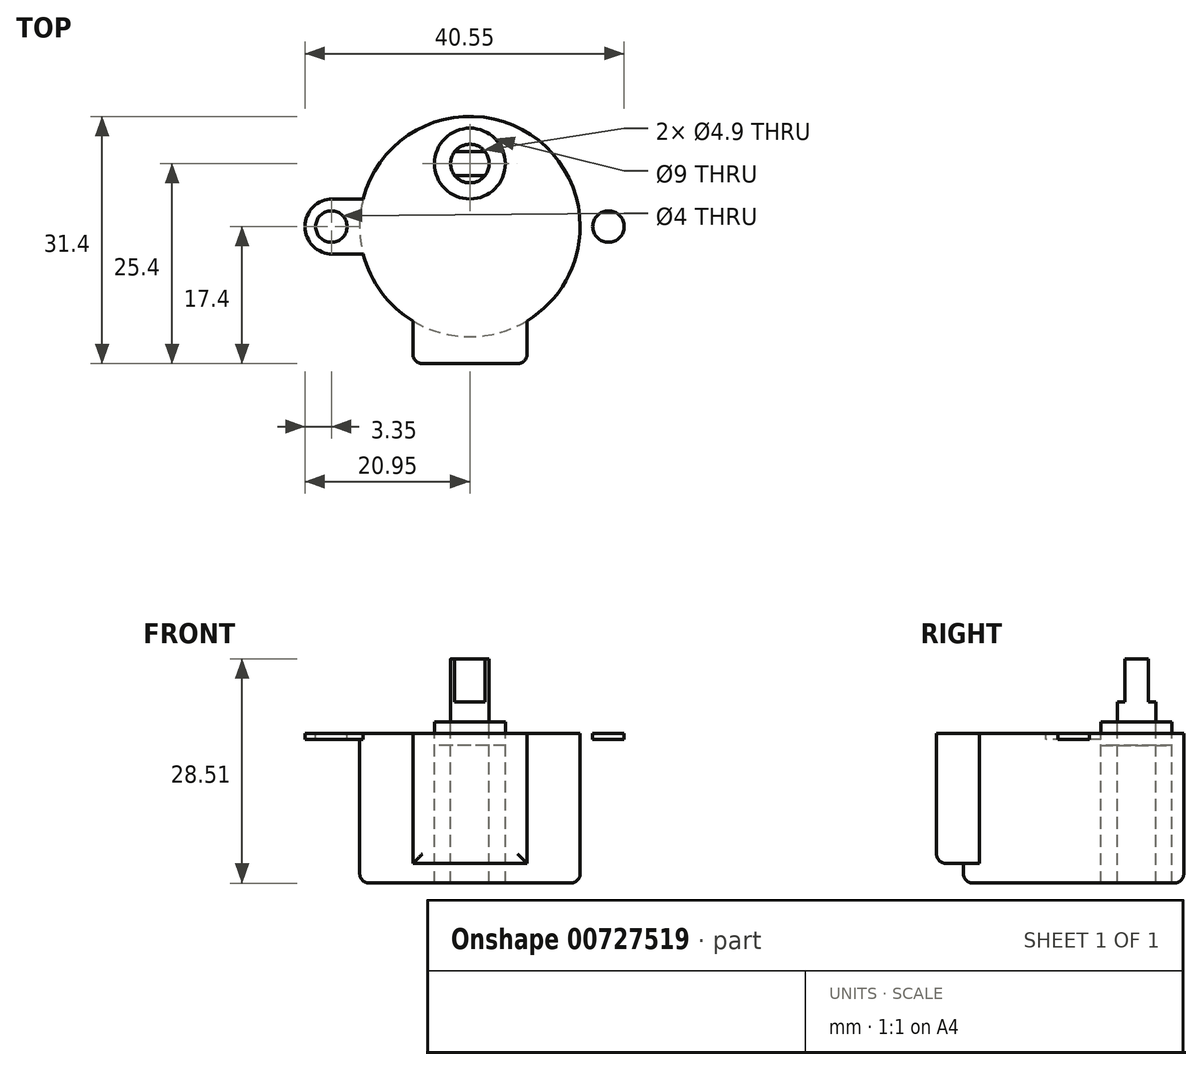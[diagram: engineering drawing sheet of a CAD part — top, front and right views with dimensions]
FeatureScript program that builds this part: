
annotation { "Feature Type Name" : "Feature", "Feature Type Description" : "" }
export const myFeature = defineFeature(function(context is Context, id is Id, definition is map)
    precondition{}
    {
        {
            var Q0;
            Q0=qCreatedBy(makeId("Top.planeOp"),FACE);
            var sketch = newSketch(context, id + "F0", { "sketchPlane" : qUnion([Q0])});
            skCircle(sketch, "E0", {"center": v(0, 0) * mm, "radius": 14 * mm});
            skPoint(sketch, "E1", {"position": v(0, 8) * mm});
            skCircle(sketch, "E2", {"center": v(0, 8) * mm, "radius": 4.5 * mm});
            skLineSegment(sketch, "E3.bottom", {"start": v(-17.45, -3.5) * mm, "end": v(-13.56, -3.5) * mm});
            skLineSegment(sketch, "E3.top", {"start": v(-17.45, 3.5) * mm, "end": v(-13.56, 3.5) * mm});
            skLineSegment(sketch, "E3.left", {"start": v(-20.95, 0) * mm, "end": v(-20.95, 0) * mm});
            skLineSegment(sketch, "E3.right", {"start": v(20.95, 0) * mm, "end": v(20.95, 0) * mm});
            skCircle(sketch, "E4", {"center": v(-17.6, 0) * mm, "radius": 2 * mm});
            skPoint(sketch, "E5.visualSharp", {"position": v(-20.95, 3.5) * mm});
            skArc(sketch, "E5.filletArc", {"start": v(-17.45, 3.5) * mm, "mid": v(-19.92, 2.47) * mm, "end": v(-20.95, 0) * mm});
            skPoint(sketch, "E6.visualSharp", {"position": v(-20.95, -3.5) * mm});
            skArc(sketch, "E6.filletArc", {"start": v(-20.95, 0) * mm, "mid": v(-19.92, -2.47) * mm, "end": v(-17.45, -3.5) * mm});
            skCircle(sketch, "E7.MirrorC", {"center": v(17.6, 0) * mm, "radius": 2 * mm});
            skArc(sketch, "E8.MirrorCS", {"start": v(20.95, 0) * mm, "mid": v(19.92, -2.47) * mm, "end": v(17.45, -3.5) * mm});
            skArc(sketch, "E9.MirrorCS", {"start": v(17.45, 3.5) * mm, "mid": v(19.92, 2.47) * mm, "end": v(20.95, 0) * mm});
            skPoint(sketch, "E10.visualSharp", {"position": v(20.95, -3.5) * mm});
            skArc(sketch, "E10.filletArc", {"start": v(17.45, -3.5) * mm, "mid": v(19.92, -2.47) * mm, "end": v(20.95, 0) * mm});
            skPoint(sketch, "E11.visualSharp", {"position": v(20.95, 3.5) * mm});
            skArc(sketch, "E11.filletArc", {"start": v(20.95, 0) * mm, "mid": v(19.92, 2.47) * mm, "end": v(17.45, 3.5) * mm});
            skCircle(sketch, "E12", {"center": v(0, 8) * mm, "radius": 2.45 * mm});
            skLineSegment(sketch, "E13.bottom", {"start": v(1.94, 6.5) * mm, "end": v(-1.94, 6.5) * mm});
            skLineSegment(sketch, "E13.top", {"start": v(1.94, 9.5) * mm, "end": v(-1.94, 9.5) * mm});
            skLineSegment(sketch, "E14.trimOffspring", {"start": v(13.56, -3.5) * mm, "end": v(17.45, -3.5) * mm});
            skLineSegment(sketch, "E15.trimOffspring", {"start": v(13.56, 3.5) * mm, "end": v(17.45, 3.5) * mm});
            skPoint(sketch, "E16", {"position": v(0, -17.4) * mm});
            skLineSegment(sketch, "E17.bottom", {"start": v(0, -17.4) * mm, "end": v(7.25, -17.4) * mm});
            skLineSegment(sketch, "E17.right", {"start": v(7.25, -17.4) * mm, "end": v(7.25, -11.98) * mm});
            skLineSegment(sketch, "E18.MirrorCS", {"start": v(0, -17.4) * mm, "end": v(-7.25, -17.4) * mm});
            skLineSegment(sketch, "E19.MirrorCS", {"start": v(-7.25, -17.4) * mm, "end": v(-7.25, -11.98) * mm});
            skPoint(sketch, "E20.orphan", {"position": v(0, -11.4) * mm});
            skPoint(sketch, "E21.orphan", {"position": v(-7.25, -11.4) * mm});
            skPoint(sketch, "E22.orphan", {"position": v(7.25, -11.4) * mm});
            skSolve(sketch);
        }
        {
            var Q0;
            {var subQ0=sQuery(id+"F0.wireOp",EDGE,"E13.bottom");Q0=makeQuery(id+"F0.imprint","IMPRINT",FACE,{"disambiguationData":[TD([[makeQuery(id+"F0.imprint","IMPRINT",EDGE,{"derivedFrom":subQ0}),-1.0]])]});}
            extrude(context, id + "F1", {"entities" : qUnion([Q0]), "depth" : 8 * mm, "offsetDistance" : 25 * mm});
        }
        {
            var Q0;
            {var subQ0=sQuery(id+"F0.wireOp",EDGE,"E13.bottom");Q0=makeQuery(id+"F0.imprint","IMPRINT",FACE,{"disambiguationData":[TD([[makeQuery(id+"F0.imprint","IMPRINT",EDGE,{"derivedFrom":subQ0}),1.0]])]});}
            var Q1;
            {var subQ0=sQuery(id+"F0.wireOp",EDGE,"E13.top");Q1=makeQuery(id+"F0.imprint","IMPRINT",FACE,{"disambiguationData":[TD([[makeQuery(id+"F0.imprint","IMPRINT",EDGE,{"derivedFrom":subQ0}),-1.0]])]});}
            extrude(context, id + "F2", {"entities" : qUnion([Q0, Q1]), "operationType" : NewBodyOperationType.ADD, "depth" : 2.5 * mm, "offsetDistance" : 25 * mm});
        }
        {
            var Q0;
            Q0=makeQuery(id+"F0.imprint","IMPRINT",FACE,{"disambiguationData":[TD([[makeQuery(id+"F0.imprint","IMPRINT",EDGE,{"derivedFrom":sQuery(id+"F0.wireOp",EDGE,"E2")}),1.0]])]});
            extrude(context, id + "F3", {"entities" : qUnion([Q0]), "depth" : -1.5 * mm, "offsetDistance" : 25 * mm});
        }
        {
            var Q0;
            Q0=makeQuery(id+"F0.imprint","IMPRINT",FACE,{"disambiguationData":[TD([[makeQuery(id+"F0.imprint","IMPRINT",EDGE,{"derivedFrom":sQuery(id+"F0.wireOp",EDGE,"E2")}),-1.0]])]});
            var Q1;
            {var subQ0=sQuery(id+"F0.wireOp",EDGE,"E13.bottom");Q1=makeQuery(id+"F0.imprint","IMPRINT",FACE,{"disambiguationData":[TD([[makeQuery(id+"F0.imprint","IMPRINT",EDGE,{"derivedFrom":subQ0}),-1.0]])]});}
            var Q2;
            {var subQ0=sQuery(id+"F0.wireOp",EDGE,"E13.bottom");Q2=makeQuery(id+"F0.imprint","IMPRINT",FACE,{"disambiguationData":[TD([[makeQuery(id+"F0.imprint","IMPRINT",EDGE,{"derivedFrom":subQ0}),1.0]])]});}
            var Q3;
            {var subQ0=sQuery(id+"F0.wireOp",EDGE,"E13.top");Q3=makeQuery(id+"F0.imprint","IMPRINT",FACE,{"disambiguationData":[TD([[makeQuery(id+"F0.imprint","IMPRINT",EDGE,{"derivedFrom":subQ0}),-1.0]])]});}
            var Q4;
            Q4=makeQuery(id+"F3.opExtrude","CAP_FACE",FACE,{"disambiguationData":[OSD([sQuery(id+"F0.wireOp",EDGE,"E2"),sQuery(id+"F0.wireOp",EDGE,"E12")])],"isStart":false});
            extrude(context, id + "F4", {"entities" : qUnion([Q0, Q1, Q2, Q3, Q4]), "oppositeDirection" : true, "depth" : 20.5 * mm, "offsetDistance" : 25 * mm, "hasSecondDirection" : true, "secondDirectionOppositeDirection" : true, "secondDirectionDepth" : 1.5 * mm});
        }
        {
            var Q0;
            {var subQ1=sQuery(id+"F0.wireOp",EDGE,"E3.bottom");Q0=makeQuery(id+"F0.imprint","IMPRINT",FACE,{"disambiguationData":[TD([[makeQuery(id+"F0.imprint","IMPRINT",EDGE,{"derivedFrom":subQ1}),1.0]])]});}
            var Q1;
            Q1=makeQuery(id+"F0.imprint","IMPRINT",FACE,{"disambiguationData":[TD([[makeQuery(id+"F0.imprint","IMPRINT",EDGE,{"derivedFrom":sQuery(id+"F0.wireOp",EDGE,"E7.MirrorC")}),1.0]])]});
            extrude(context, id + "F5", {"entities" : qUnion([Q0, Q1]), "operationType" : NewBodyOperationType.ADD, "oppositeDirection" : true, "depth" : 2.25 * mm, "offsetDistance" : 25 * mm, "hasSecondDirection" : true, "secondDirectionOppositeDirection" : true, "secondDirectionDepth" : 1.5 * mm});
        }
        {
            var Q0;
            Q0=makeQuery(id+"F0.imprint","IMPRINT",FACE,{"disambiguationData":[TD([[makeQuery(id+"F0.imprint","IMPRINT",EDGE,{"derivedFrom":sQuery(id+"F0.wireOp",EDGE,"E17.bottom")}),1.0]])]});
            extrude(context, id + "F6", {"entities" : qUnion([Q0]), "operationType" : NewBodyOperationType.ADD, "oppositeDirection" : true, "depth" : 18 * mm, "offsetDistance" : 25 * mm, "hasSecondDirection" : true, "secondDirectionOppositeDirection" : true, "secondDirectionDepth" : 1.5 * mm});
        }
        {
            var Q0;
            Q0=qCreatedBy(makeId("Right.planeOp"),FACE);
            var sketch = newSketch(context, id + "F7", { "sketchPlane" : qUnion([Q0])});
            skLineSegment(sketch, "E23.bottom", {"start": v(3.11, -20.5) * mm, "end": v(12.88, -20.5) * mm});
            skLineSegment(sketch, "E23.top", {"start": v(3.11, -23.57) * mm, "end": v(12.88, -23.57) * mm});
            skLineSegment(sketch, "E23.left", {"start": v(3.11, -20.5) * mm, "end": v(3.11, -23.57) * mm});
            skLineSegment(sketch, "E23.right", {"start": v(12.88, -20.5) * mm, "end": v(12.88, -23.57) * mm});
            skSolve(sketch);
        }
        {
            var Q0;
            Q0 = qSketchRegion(id + "F7", true);
            extrude(context, id + "F8", {"entities" : qUnion([Q0]), "operationType" : NewBodyOperationType.REMOVE, "oppositeDirection" : true, "depth" : 50 * mm, "offsetDistance" : 25 * mm, "hasSecondDirection" : true, "secondDirectionOppositeDirection" : false, "secondDirectionDepth" : 25 * mm});
        }
        {
            var Q0;
            Q0=makeQuery(id+"F6.opExtrude","SWEPT_EDGE",EDGE,{"disambiguationData":[OSD([sQuery(id+"F0.wireOp",EDGE,"E18.MirrorCS"),sQuery(id+"F0.wireOp",EDGE,"E19.MirrorCS")])]});
            var Q1;
            Q1=makeQuery(id+"F6.opExtrude","CAP_EDGE",EDGE,{"disambiguationData":[OSD([sQuery(id+"F0.wireOp",EDGE,"E17.bottom"),sQuery(id+"F0.wireOp",EDGE,"E18.MirrorCS")])],"isStart":false});
            var Q2;
            Q2=makeQuery(id+"F6.opExtrude","SWEPT_EDGE",EDGE,{"disambiguationData":[OSD([sQuery(id+"F0.wireOp",EDGE,"E17.bottom"),sQuery(id+"F0.wireOp",EDGE,"E17.right")])]});
            var Q3;
            Q3=makeQuery(id+"F4.opExtrude","CAP_EDGE",EDGE,{"disambiguationData":[OSD([sQuery(id+"F0.wireOp",EDGE,"E0")])],"isStart":false});
            fillet(context, id + "F9", {"entities" : qUnion([Q0, Q1, Q2, Q3]), "radius" : 1.2 * mm, "tangentPropagation" : true, "allowEdgeOverflow" : false});
        }
    });
